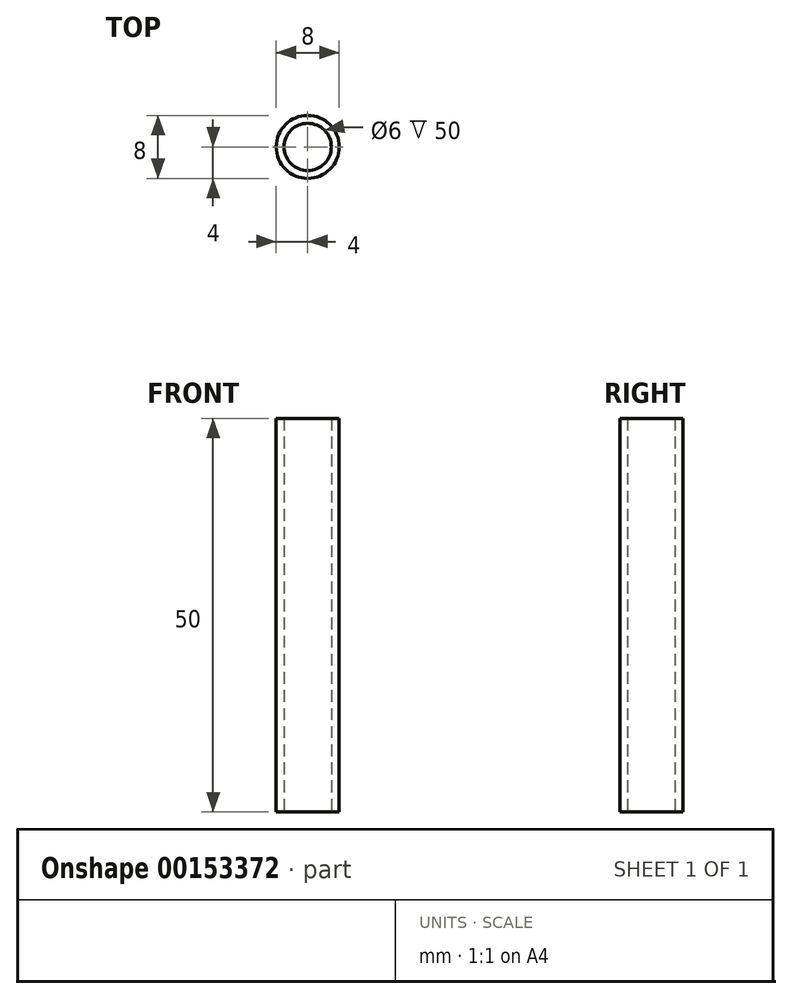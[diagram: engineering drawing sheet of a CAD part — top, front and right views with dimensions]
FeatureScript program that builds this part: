
annotation { "Feature Type Name" : "Feature", "Feature Type Description" : "" }
export const myFeature = defineFeature(function(context is Context, id is Id, definition is map)
    precondition{}
    {
        {
            var Q0;
            Q0=qCreatedBy(makeId("Top.planeOp"),FACE);
            var sketch = newSketch(context, id + "F0", { "sketchPlane" : qUnion([Q0])});
            skCircle(sketch, "E0", {"center": v(0, 0) * mm, "radius": 4 * mm});
            skCircle(sketch, "E1", {"center": v(0, 0) * mm, "radius": 3 * mm});
            skSolve(sketch);
        }
        {
            var Q0;
            Q0 = qSketchRegion(id + "F0", true);
            extrude(context, id + "F1", {"entities" : qUnion([Q0]), "depth" : 50 * mm});
        }
    });
